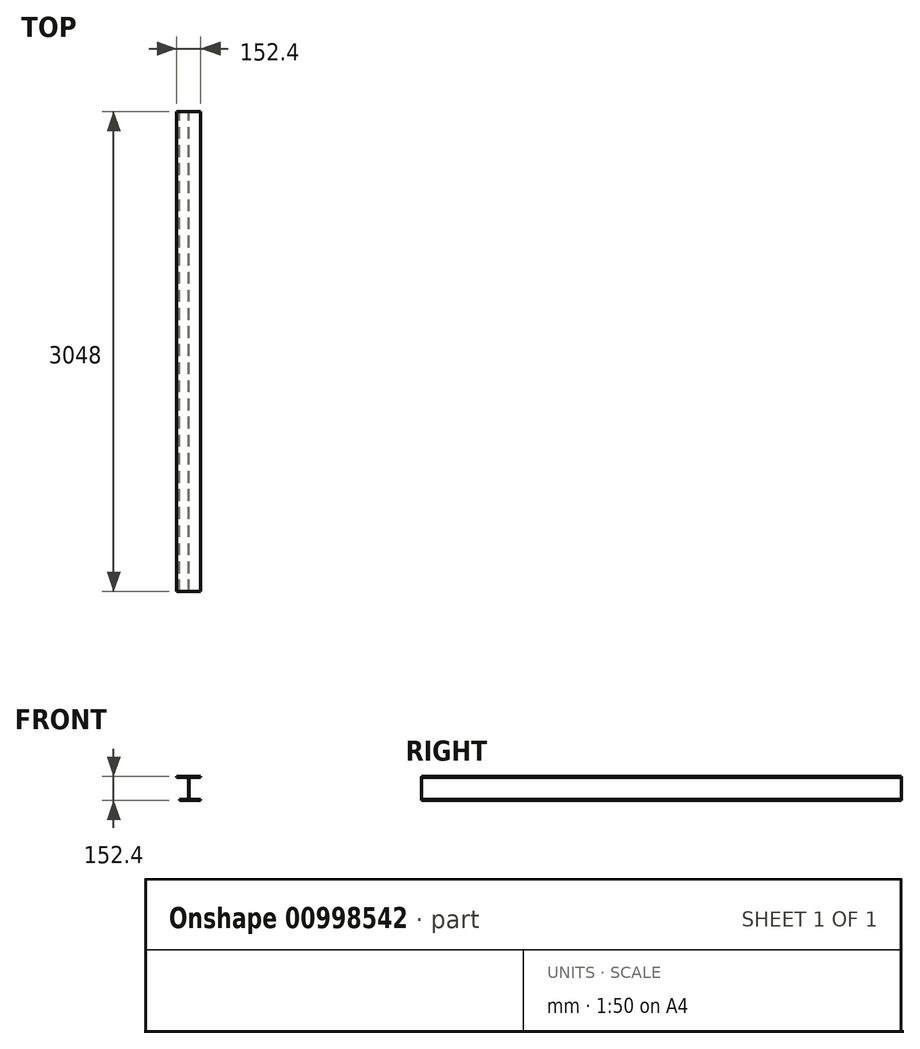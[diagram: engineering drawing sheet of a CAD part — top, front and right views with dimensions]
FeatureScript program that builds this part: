
annotation { "Feature Type Name" : "Feature", "Feature Type Description" : "" }
export const myFeature = defineFeature(function(context is Context, id is Id, definition is map)
    precondition{}
    {
        {
            var Q0;
            Q0=qCreatedBy(makeId("Front.planeOp"),FACE);
            var sketch = newSketch(context, id + "F0", { "sketchPlane" : qUnion([Q0])});
            skLineSegment(sketch, "E0", {"start": v(-76.2, 0) * mm, "end": v(76.2, 0) * mm});
            skLineSegment(sketch, "E1", {"start": v(-59.54, -152.4) * mm, "end": v(75.94, -152.4) * mm});
            skLineSegment(sketch, "E2", {"start": v(-76.2, 0) * mm, "end": v(-76.2, -5) * mm});
            skLineSegment(sketch, "E3", {"start": v(-76.2, -5) * mm, "end": v(-2.5, -5) * mm});
            skLineSegment(sketch, "E4", {"start": v(-2.5, -5) * mm, "end": v(-2.5, -147.4) * mm});
            skLineSegment(sketch, "E5", {"start": v(76.2, 0) * mm, "end": v(76.2, -5) * mm});
            skLineSegment(sketch, "E6", {"start": v(76.2, -5) * mm, "end": v(2.5, -5) * mm});
            skLineSegment(sketch, "E7", {"start": v(2.5, -5) * mm, "end": v(2.5, -147.4) * mm});
            skLineSegment(sketch, "E8", {"start": v(2.5, -147.4) * mm, "end": v(75.94, -147.4) * mm});
            skLineSegment(sketch, "E9", {"start": v(75.94, -147.4) * mm, "end": v(75.94, -152.4) * mm});
            skLineSegment(sketch, "E10", {"start": v(-2.5, -147.4) * mm, "end": v(-59.3, -147.4) * mm});
            skLineSegment(sketch, "E11", {"start": v(-59.3, -147.4) * mm, "end": v(-59.3, -152.4) * mm});
            skSolve(sketch);
        }
        {
            var Q0;
            Q0 = qSketchRegion(id + "F0", true);
            extrude(context, id + "F1", {"entities" : qUnion([Q0]), "depth" : 3048 * mm, "offsetDistance" : 25.4 * mm});
        }
    });
